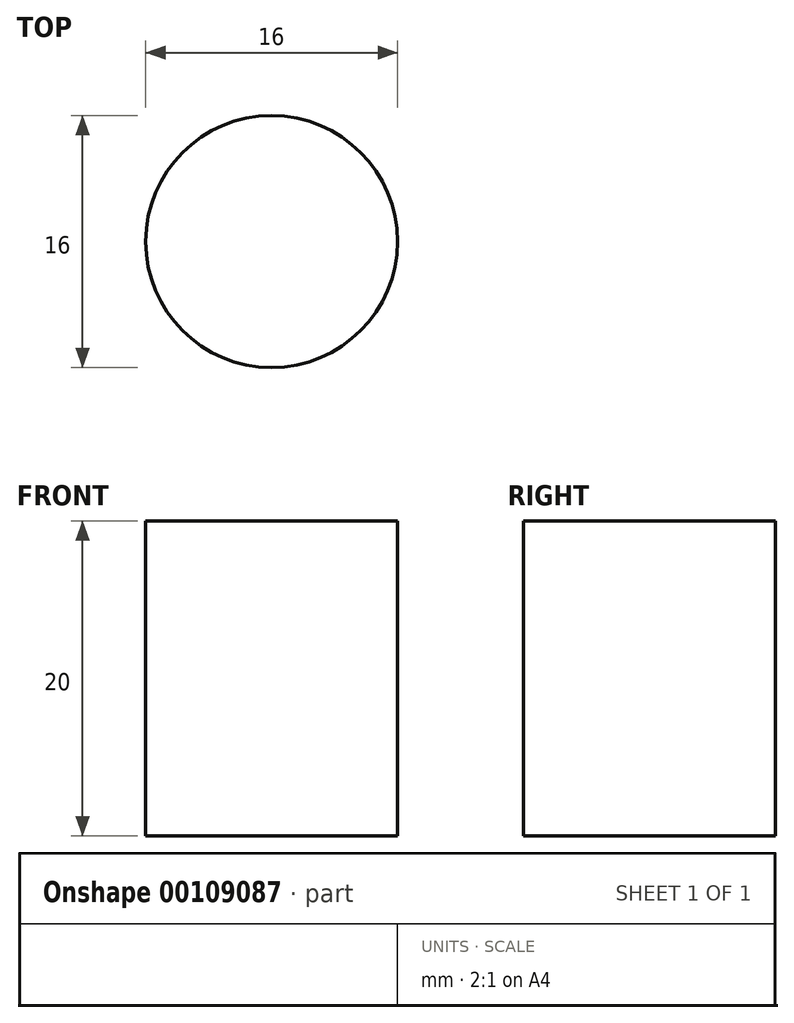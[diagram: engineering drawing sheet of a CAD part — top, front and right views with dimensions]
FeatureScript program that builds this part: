
annotation { "Feature Type Name" : "Feature", "Feature Type Description" : "" }
export const myFeature = defineFeature(function(context is Context, id is Id, definition is map)
    precondition{}
    {
        {
            var Q0;
            Q0=qCreatedBy(makeId("Top.planeOp"),FACE);
            var sketch = newSketch(context, id + "F0", { "sketchPlane" : qUnion([Q0])});
            skCircle(sketch, "E0", {"center": v(0, 0) * mm, "radius": 8 * mm});
            skSolve(sketch);
        }
        {
            var Q0;
            Q0=makeQuery(id+"F0.imprint","IMPRINT",FACE,{"disambiguationData":[TD([[makeQuery(id+"F0.imprint","IMPRINT",EDGE,{"derivedFrom":sQuery(id+"F0.wireOp",EDGE,"E0")}),1.0]])]});
            extrude(context, id + "F1", {"entities" : qUnion([Q0]), "depth" : 20 * mm});
        }
    });
